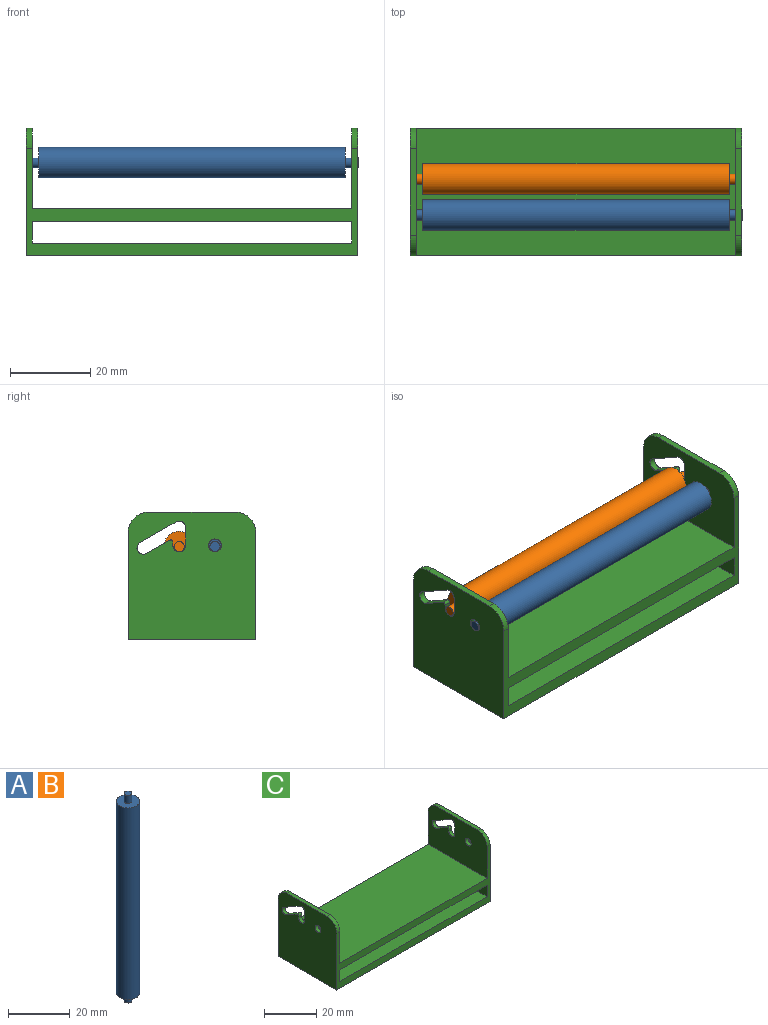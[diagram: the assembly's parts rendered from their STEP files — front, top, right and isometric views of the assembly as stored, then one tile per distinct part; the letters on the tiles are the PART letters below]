
ASSEMBLY  parts=3 mates=1
PART A: 7 faces, bbox 7.6x7.6x82.6 mm
  f0: cylinder r=3.81mm len=76.2mm, axis (0,0,-1), area 1824.1mm2, adj f1,f2
  f1: plane 7.62x7.62mm, normal (0,0,1), area 40.5mm2, adj f0,f5
  f2: plane 7.62x7.62mm, normal (0,0,-1), area 40.5mm2, adj f0,f4
  f3: plane 2.54x2.54mm, normal (0,0,-1), area 5.1mm2, adj f4
  f4: cylinder r=1.27mm len=3.18mm, axis (0,0,-1), area 25.3mm2, adj f2,f3
  f5: cylinder r=1.27mm len=3.18mm, axis (0,0,-1), area 25.3mm2, adj f1,f6
  f6: plane 2.54x2.54mm, normal (0,0,1), area 5.1mm2, adj f5
PART B: same geometry as A
PART C: 36 faces, bbox 82.6x31.8x31.8 mm
  f0: plane 79.38x31.75mm, normal (0,0,-1), area 2520.2mm2, adj f1,f11,f12,f13
  f1: plane 31.75x5.4mm, normal (-1,0,0), area 171.4mm2, adj f0,f2,f12,f13
  f2: plane 79.38x31.75mm, normal (0,0,1), area 2520.2mm2, adj f1,f11,f12,f13
  f3: plane 31.75x31.75mm, normal (-1,0,0), area 936mm2, adj f4,f10,f12,f13,f14,f15,f16,f17
  f4: plane 82.55x31.75mm, normal (0,0,-1), area 2621mm2, adj f3,f5,f12,f13
  f5: plane 31.75x31.75mm, normal (1,0,0), area 936mm2, adj f4,f6,f12,f13,f23,f24,f25,f26
  f6: plane 21.59x1.59mm, normal (0,0,1), area 34.3mm2, adj f5,f7,f33,f35
  f7: plane 31.75x20mm, normal (-1,0,0), area 563mm2, adj f6,f8,f12,f13,f23,f24,f25,f26
  f8: plane 79.38x31.75mm, normal (0,0,1), area 2520.2mm2, adj f7,f9,f12,f13
  f9: plane 31.75x20mm, normal (1,0,0), area 563mm2, adj f8,f10,f12,f13,f14,f15,f16,f17
  f10: plane 21.59x1.59mm, normal (0,0,1), area 34.3mm2, adj f3,f9,f32,f34
  f11: plane 31.75x5.4mm, normal (1,0,0), area 171.4mm2, adj f0,f2,f12,f13
  f12: plane 82.55x26.67mm, normal (0,-1,0), area 588.7mm2, adj f0,f1,f2,f3,f4,f5,f7,f8
  f13: plane 82.55x26.67mm, normal (0,1,0), area 588.7mm2, adj f0,f1,f2,f3,f4,f5,f7,f8
  f14: cylinder r=1.59mm len=3.18mm, axis (-1,0,0), area 15.8mm2, adj f3,f9
  f15: cylinder r=1.59mm len=3.18mm, axis (-1,0,0), area 7.9mm2, adj f3,f9,f16,f22
  f16: plane 1.59x0.85mm, normal (0,-1,0), area 1.3mm2, adj f3,f9,f15,f17
  f17: cylinder r=0.51mm len=1.59mm, axis (-1,0,0), area 1.7mm2, adj f3,f9,f16,f18
  f18: plane 5.79x3.28mm, normal (0,0.49,0.87), area 10.6mm2, adj f3,f9,f17,f19
  f19: cylinder r=1.59mm len=2.97mm, axis (-1,0,0), area 7.9mm2, adj f3,f9,f18,f20
  f20: plane 8.92x5.06mm, normal (0,-0.49,-0.87), area 16.3mm2, adj f3,f9,f19,f21
  f21: cylinder r=1.59mm len=2.37mm, axis (-1,0,0), area 5.3mm2, adj f3,f9,f20,f22
  f22: plane 4.45x1.59mm, normal (0,1,0), area 7.1mm2, adj f3,f9,f15,f21
  f23: cylinder r=1.59mm len=3.18mm, axis (-1,0,0), area 15.8mm2, adj f5,f7
  f24: plane 4.45x1.59mm, normal (0,1,0), area 7.1mm2, adj f5,f7,f25,f31
  f25: cylinder r=1.59mm len=2.37mm, axis (-1,0,0), area 5.3mm2, adj f5,f7,f24,f26
  f26: plane 8.92x5.06mm, normal (0,-0.49,-0.87), area 16.3mm2, adj f5,f7,f25,f27
  f27: cylinder r=1.59mm len=2.97mm, axis (-1,0,0), area 7.9mm2, adj f5,f7,f26,f28
  f28: plane 5.79x3.28mm, normal (0,0.49,0.87), area 10.6mm2, adj f5,f7,f27,f29
  f29: cylinder r=0.51mm len=1.59mm, axis (-1,0,0), area 1.7mm2, adj f5,f7,f28,f30
  f30: plane 1.59x0.85mm, normal (0,-1,0), area 1.3mm2, adj f5,f7,f29,f31
  f31: cylinder r=1.59mm len=3.18mm, axis (-1,0,0), area 7.9mm2, adj f5,f7,f24,f30
  f32: cylinder r=5.08mm len=5.08mm, axis (-1,0,0), area 12.7mm2, adj f3,f9,f10,f13
  f33: cylinder r=5.08mm len=5.08mm, axis (-1,0,0), area 12.7mm2, adj f5,f6,f7,f13
  f34: cylinder r=5.08mm len=5.08mm, axis (1,0,0), area 12.7mm2, adj f3,f9,f10,f12
  f35: cylinder r=5.08mm len=5.08mm, axis (1,0,0), area 12.7mm2, adj f5,f6,f7,f12
PLACE A rot(axis=(0.71,0,-0.71),180deg) t=(-15.37,-3.78,27.37)mm
PLACE B rot(axis=(0,1,0),90deg) t=(-15.37,5.11,27.37)mm
PLACE C t=(-15.37,1.94,4.19)mm
MATE pin_slot A.f4 <-> C.f14  axis (-1,0,0) through (-56.64,-3.78,27.37)mm
